# Revit family: CACLI
name_source: partatom
category: Air Terminals
revit_build: Autodesk Revit MEP 2012 (Build: 20110309_2315(x64)
units: mm (PartAtom-declared; Revit-internal decimal feet)

## types (3) — shared parameters
Conect_Cuello = 22 1/2"
Description = Difusor tipo cuadrilineal
Función = Inyección
Manufacturer = INNES
Material = Aluminio
Model = CACLI
Nota_1 = .
Posición de Instalación = Muro/Techo
Ranuras Disponibles = 1 a 3 ranuras
Separación entre Ranuras = de 3/4"
Tamaño de Construcción = únicamente en módulo de 24"x24"
Tipo de Cuello = Cuadrado
Type Comments = Patrón de aire ajustable
URL = https://www.innes.com.mx
Visible_Texto = No

## per-type parameters (varying)
| type | N°_Ranuras | Perfil_1 | Perfil_2 | Redondo_1 | Redondo_2 | Redondos |
| CACLI_1-Ranura | 1 | No | No | No | Yes | No |
| CACLI_2-Ranuras | 2 | No | Yes | Yes | No | No |
| CACLI_3-Ranuras | 3 | Yes | Yes | No | No | Yes |

## geometry (parser evidence)
native form markers: Sweep x4
no freeform markers — native parametric forms only
